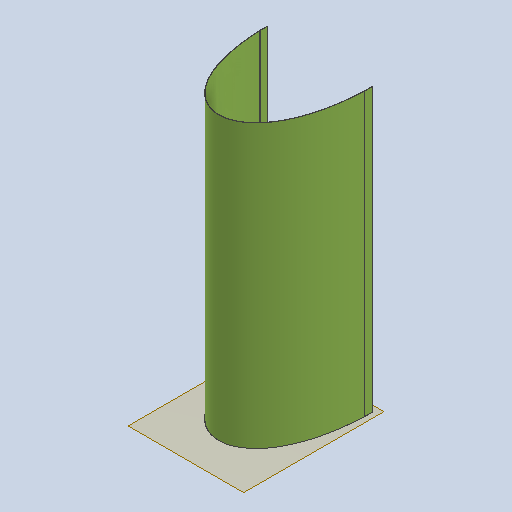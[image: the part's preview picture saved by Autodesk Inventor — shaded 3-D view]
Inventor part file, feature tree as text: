
AUTODESK INVENTOR PART (.ipt)
format: ipt  version: 2023 (Build 270158030, 158C)  size: 118,272 bytes
history: native  units: mm
features: other x3, plane x2, reference x2, sketch x1, extrude x1
ambient origin geometry x8: Origin, YZ Plane, XZ Plane, XY Plane, X Axis, Y Axis, Z Axis, Center Point
bodies: Body1 (feature_tree)
feature tree (9):
  other  "cover-deployed"
  plane  "Work Plane1"
  sketch  "Sketch1"  dims[d0=2.0mm d1=10.0mm d2=0.0mm]
  plane  "Work Plane2"
  extrude  "Extrusion1"  Depth=10.0mm TaperAngle=0.0deg
  reference  "Reference1"
  reference  "Reference2"
  other  "primary-engineer-bench.iam"
  other  "back-flaps-3:2"
